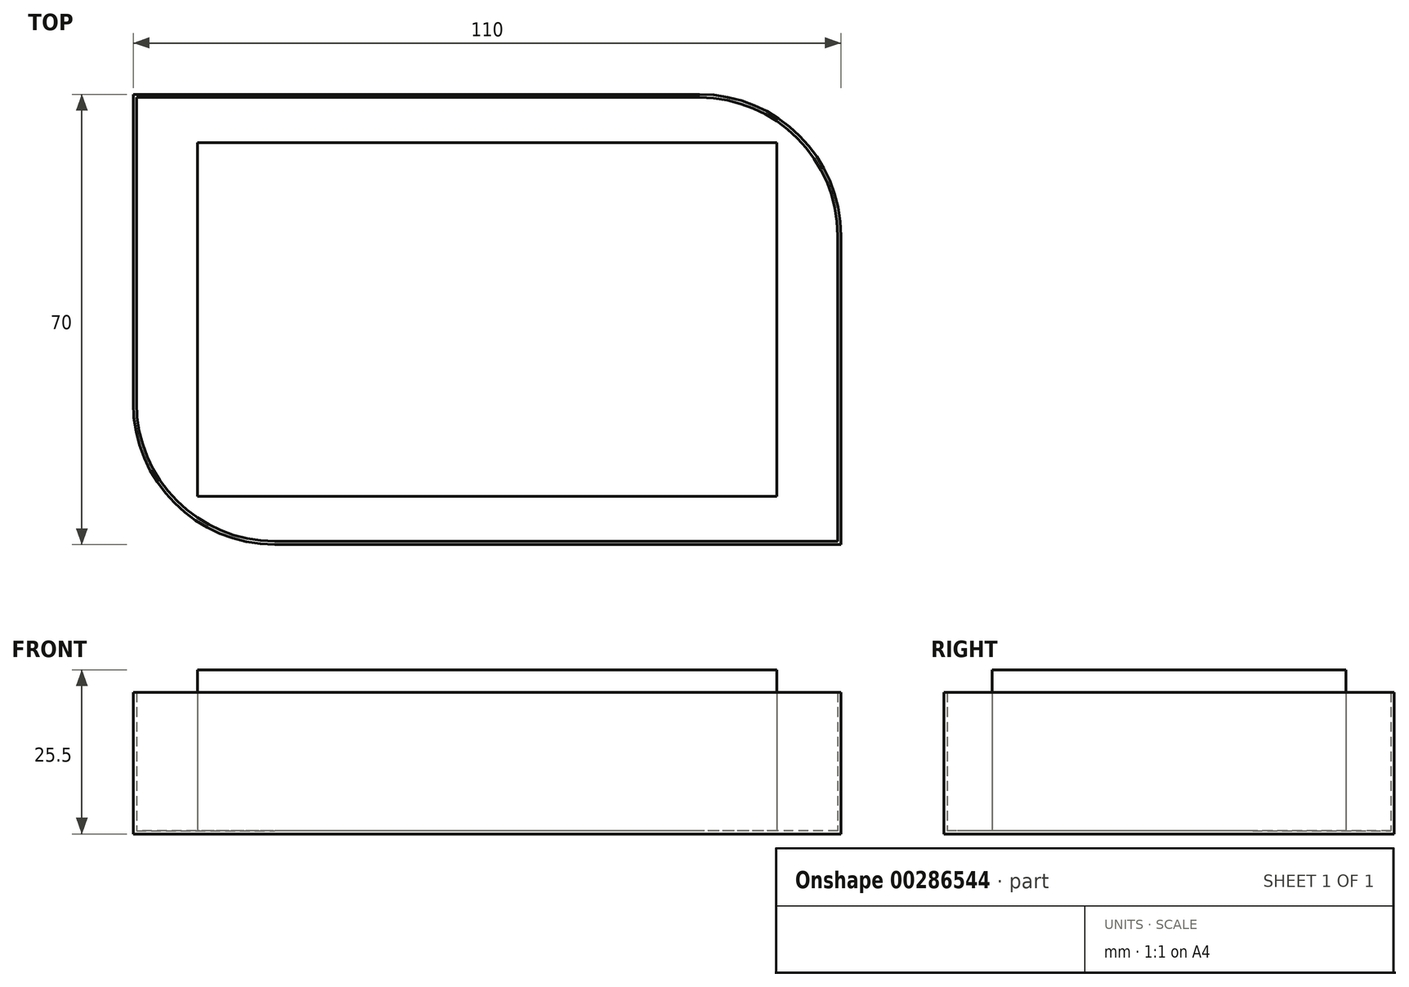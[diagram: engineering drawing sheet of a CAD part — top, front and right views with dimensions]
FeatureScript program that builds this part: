
annotation { "Feature Type Name" : "Feature", "Feature Type Description" : "" }
export const myFeature = defineFeature(function(context is Context, id is Id, definition is map)
    precondition{}
    {
        {
            var Q0;
            Q0=qCreatedBy(makeId("Top.planeOp"),FACE);
            var sketch = newSketch(context, id + "F0", { "sketchPlane" : qUnion([Q0])});
            skLineSegment(sketch, "E0.bottom", {"start": v(33, 35) * mm, "end": v(-55, 35) * mm});
            skLineSegment(sketch, "E0.top", {"start": v(55, -35) * mm, "end": v(-33, -35) * mm});
            skLineSegment(sketch, "E0.left", {"start": v(55, 13) * mm, "end": v(55, -35) * mm});
            skLineSegment(sketch, "E0.right", {"start": v(-55, 35) * mm, "end": v(-55, -13) * mm});
            skPoint(sketch, "E0.middle", {"position": v(0, 0) * mm});
            skPoint(sketch, "E1.visualSharp", {"position": v(55, 35) * mm});
            skArc(sketch, "E1.filletArc", {"start": v(55, 13) * mm, "mid": v(48.56, 28.56) * mm, "end": v(33, 35) * mm});
            skPoint(sketch, "E2.visualSharp", {"position": v(-55, -35) * mm});
            skArc(sketch, "E2.filletArc", {"start": v(-55, -13) * mm, "mid": v(-48.56, -28.56) * mm, "end": v(-33, -35) * mm});
            skSolve(sketch);
        }
        {
            var Q0;
            Q0=qSketchRegion(id+"F0",true);
            extrude(context, id + "F1", {"entities" : qUnion([Q0]), "depth" : 22 * mm});
        }
        {
            var Q0;
            Q0=makeQuery(id+"F1.opExtrude","CAP_FACE",FACE,{"disambiguationData":[OSD([sQuery(id+"F0.wireOp",EDGE,"E0.bottom"),sQuery(id+"F0.wireOp",EDGE,"E0.top"),sQuery(id+"F0.wireOp",EDGE,"E0.left"),sQuery(id+"F0.wireOp",EDGE,"E0.right"),sQuery(id+"F0.wireOp",EDGE,"E1.filletArc"),sQuery(id+"F0.wireOp",EDGE,"E2.filletArc")])],"isStart":false});
            shell(context, id + "F2", {"entities" : qUnion([Q0]), "thickness" : .5 * mm});
        }
        {
            var Q0;
            Q0=makeQuery(id+"F2.opShell","OFFSET_FACE",FACE,{"disambiguationData":[OSD([sQuery(id+"F0.wireOp",EDGE,"E0.bottom"),sQuery(id+"F0.wireOp",EDGE,"E0.top"),sQuery(id+"F0.wireOp",EDGE,"E0.left"),sQuery(id+"F0.wireOp",EDGE,"E0.right"),sQuery(id+"F0.wireOp",EDGE,"E1.filletArc"),sQuery(id+"F0.wireOp",EDGE,"E2.filletArc")])]});
            var sketch = newSketch(context, id + "F3", { "sketchPlane" : qUnion([Q0])});
            skLineSegment(sketch, "E3.bottom", {"start": v(45, 27.5) * mm, "end": v(-45, 27.5) * mm});
            skLineSegment(sketch, "E3.top", {"start": v(45, -27.5) * mm, "end": v(-45, -27.5) * mm});
            skLineSegment(sketch, "E3.left", {"start": v(45, 27.5) * mm, "end": v(45, -27.5) * mm});
            skLineSegment(sketch, "E3.right", {"start": v(-45, 27.5) * mm, "end": v(-45, -27.5) * mm});
            skPoint(sketch, "E3.middle", {"position": v(0, 0) * mm});
            skSolve(sketch);
        }
        {
            var Q0;
            Q0 = qSketchRegion(id + "F3", true);
            extrude(context, id + "F4", {"entities" : qUnion([Q0]), "depth" : 25 * mm});
        }
    });
